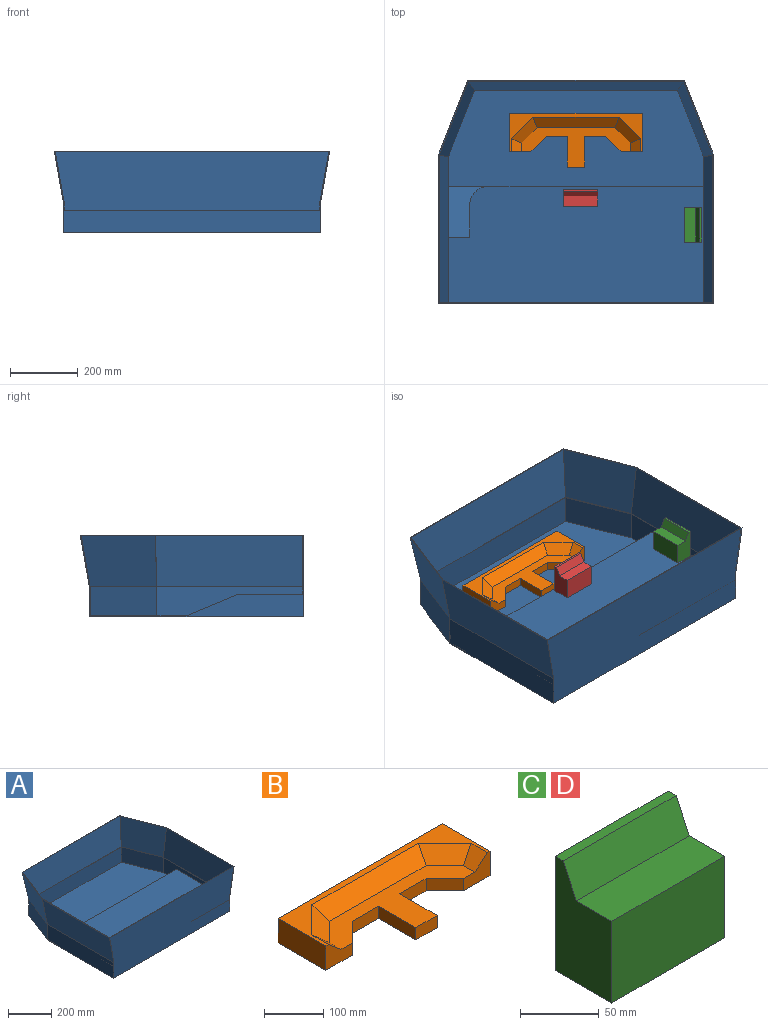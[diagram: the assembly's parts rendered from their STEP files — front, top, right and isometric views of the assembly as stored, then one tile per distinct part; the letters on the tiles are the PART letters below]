
ASSEMBLY  parts=4 mates=3
PART A: 30 faces, bbox 815.7x661.9x241.3 mm
  f0: plane 756.92x345.71mm, normal (0,0,1), area 251377.7mm2, adj f17,f18,f22,f26,f27,f28,f29
  f1: plane 756.92x284.21mm, normal (0,0,1), area 199784.9mm2, adj f18,f19,f20,f21,f22,f26,f27
  f2: plane 815.74x661.87mm, normal (0,0,1), area 7201.8mm2, adj f3,f4,f5,f12,f13,f14,f15,f16
  f3: plane 440.24x152.4mm, normal (0.98,0,-0.17), area 67733.9mm2, adj f2,f5,f6,f12
  f4: plane 440.24x152.4mm, normal (-0.98,0,-0.17), area 67733.9mm2, adj f2,f5,f10,f14
  f5: plane 815.74x241.3mm, normal (0,-1,0), area 187965.9mm2, adj f2,f3,f4,f6,f10,f11
  f6: plane 435.16x88.9mm, normal (1,0,0), area 38685.3mm2, adj f3,f5,f7,f11
  f7: plane 199.84x88.9mm, normal (0.93,0.37,0), area 19083.6mm2, adj f6,f8,f11,f12
  f8: plane 605.25x88.9mm, normal (0,1,0), area 53806.4mm2, adj f7,f9,f11,f13
  f9: plane 199.84x88.9mm, normal (-0.93,0.37,0), area 19083.6mm2, adj f8,f10,f11,f14
  f10: plane 435.16x88.9mm, normal (-1,0,0), area 38685.3mm2, adj f4,f5,f9,f11
  f11: plane 762x635mm, normal (0,0,-1), area 468206.8mm2, adj f5,f6,f7,f8,f9,f10
  f12: plane 226.72x152.4mm, normal (0.92,0.36,-0.17), area 35030.6mm2, adj f2,f3,f7,f13
  f13: plane 641.9x152.4mm, normal (0,0.98,-0.17), area 96498.5mm2, adj f2,f8,f12,f14
  f14: plane 226.72x152.4mm, normal (-0.92,0.36,-0.17), area 35030.6mm2, adj f2,f4,f9,f13
  f15: plane 437.21x152.18mm, normal (-0.98,0,0.17), area 67167.9mm2, adj f2,f17,f18,f23
  f16: plane 437.21x152.18mm, normal (0.98,0,0.17), area 67167.9mm2, adj f2,f17,f22,f25
  f17: plane 810.59x175.26mm, normal (0,1,0), area 136741.2mm2, adj f0,f2,f15,f16,f18,f22
  f18: plane 432.14x86.58mm, normal (-1,0,0), area 15462.9mm2, adj f0,f1,f15,f17,f19,f26
  f19: plane 197.78x86.58mm, normal (-0.93,-0.37,0), area 18394.5mm2, adj f1,f18,f20,f23
  f20: plane 601.78x86.58mm, normal (0,-1,0), area 52103.6mm2, adj f1,f19,f21,f24
  f21: plane 197.78x86.58mm, normal (0.93,-0.37,0), area 18394.5mm2, adj f1,f20,f22,f25
  f22: plane 432.14x86.58mm, normal (1,0,0), area 20261.1mm2, adj f0,f1,f16,f17,f21,f27
  f23: plane 224.62x152.18mm, normal (-0.92,-0.36,0.17), area 34635mm2, adj f2,f15,f19,f24
  f24: plane 638.38x152.18mm, normal (0,-0.98,0.17), area 95818.3mm2, adj f2,f20,f23,f25
  f25: plane 224.62x152.18mm, normal (0.92,-0.36,0.17), area 34635mm2, adj f2,f16,f21,f24
  f26: plane 636.39x63.5mm, normal (0,1,0), area 40410.9mm2, adj f0,f1,f18,f29
  f27: plane 151.13x120.53mm, normal (0,0.39,0.92), area 11166.2mm2, adj f0,f1,f22,f28,f29
  f28: plane 94.1x39.54mm, normal (-1,0,0), area 1860.2mm2, adj f0,f27,f29
  f29: cylinder r=57.03mm len=63.5mm, axis (0,0,1), area 4908.3mm2, adj f0,f26,f27,f28
PART B: 20 faces, bbox 393.7x159x50.8 mm
  f0: plane 89.6x25.4mm, normal (-1,0,0), area 2275.8mm2, adj f1,f6,f7,f8
  f1: plane 50.8x25.4mm, normal (0,-1,0), area 1290.3mm2, adj f0,f7,f8,f13
  f2: plane 393.7x50.8mm, normal (0,1,0), area 20000mm2, adj f3,f8,f12,f14
  f3: plane 114.3x50.8mm, normal (-1,0,0), area 5806.4mm2, adj f2,f4,f8,f12
  f4: plane 63.5x50.8mm, normal (0,-1,0), area 2157.1mm2, adj f3,f5,f7,f8,f9,f12
  f5: plane 44.9x44.9mm, normal (0.71,-0.71,0), area 1612.9mm2, adj f4,f6,f7,f8
  f6: plane 63.05x25.4mm, normal (0,-1,0), area 1601.4mm2, adj f0,f5,f7,f8
  f7: plane 320.58x116.54mm, normal (0,0,1), area 15607.6mm2, adj f0,f1,f4,f5,f6,f9,f10,f11
  f8: plane 393.7x159mm, normal (0,0,-1), area 39592.4mm2, adj f0,f1,f2,f3,f4,f5,f6,f13
  f9: plane 39.48x30.27mm, normal (0.64,0,0.77), area 1312.3mm2, adj f4,f7,f10,f12
  f10: plane 75.17x75.17mm, normal (0.45,-0.45,0.77), area 3004.7mm2, adj f7,f9,f11,f12
  f11: plane 255.86x30.27mm, normal (0,-0.64,0.77), area 9614.8mm2, adj f7,f10,f12,f19
  f12: plane 393.7x114.3mm, normal (0,0,1), area 10005.4mm2, adj f2,f3,f4,f9,f10,f11,f14,f15
  f13: plane 89.6x25.4mm, normal (1,0,0), area 2275.8mm2, adj f1,f7,f8,f17
  f14: plane 114.3x50.8mm, normal (1,0,0), area 5806.4mm2, adj f2,f8,f12,f15
  f15: plane 63.5x50.8mm, normal (0,-1,0), area 2157.1mm2, adj f7,f8,f12,f14,f16,f18
  f16: plane 44.9x44.9mm, normal (-0.71,-0.71,0), area 1612.9mm2, adj f7,f8,f15,f17
  f17: plane 63.05x25.4mm, normal (0,-1,0), area 1601.4mm2, adj f7,f8,f13,f16
  f18: plane 39.48x30.27mm, normal (-0.64,0,0.77), area 1312.3mm2, adj f7,f12,f15,f19
  f19: plane 75.17x75.17mm, normal (-0.45,-0.45,0.77), area 3004.7mm2, adj f7,f11,f12,f18
PART C: 8 faces, bbox 101.6x50.8x88.9 mm
  f0: plane 88.9x50.8mm, normal (1,0,0), area 3555.3mm2, adj f1,f3,f4,f5,f6,f7
  f1: plane 101.6x88.9mm, normal (0,1,0), area 9032.2mm2, adj f0,f2,f5,f7
  f2: plane 88.9x50.8mm, normal (-1,0,0), area 3555.3mm2, adj f1,f3,f4,f5,f6,f7
  f3: plane 101.6x63.5mm, normal (0,-1,0), area 6451.6mm2, adj f0,f2,f4,f5
  f4: plane 101.6x31.91mm, normal (0,0,1), area 3241.7mm2, adj f0,f2,f3,f6
  f5: plane 101.6x50.8mm, normal (0,0,-1), area 5161.3mm2, adj f0,f1,f2,f3
  f6: plane 101.6x25.4mm, normal (0,-0.91,0.42), area 2847.4mm2, adj f0,f2,f4,f7
  f7: plane 101.6x7.05mm, normal (0,0,1), area 716.2mm2, adj f0,f1,f2,f6
PART D: same geometry as C
PLACE A at identity fixed
PLACE B t=(0,-40.14,2.54)mm
PLACE C rot(axis=(0,0,-1),90deg) t=(347.71,-95.49,66.04)mm
PLACE D t=(14.07,-15.5,66.04)mm
MATE fastened B.f8 <-> A.f1  axis (0,0,1) through (0,155.52,2.54)mm
MATE fastened A.f0 <-> D.f5  axis (0,0,1) through (14.07,-15.5,66.04)mm
MATE planar C.f5 <-> A.f0  axis (0,0,-1) through (347.71,-95.49,66.04)mm
